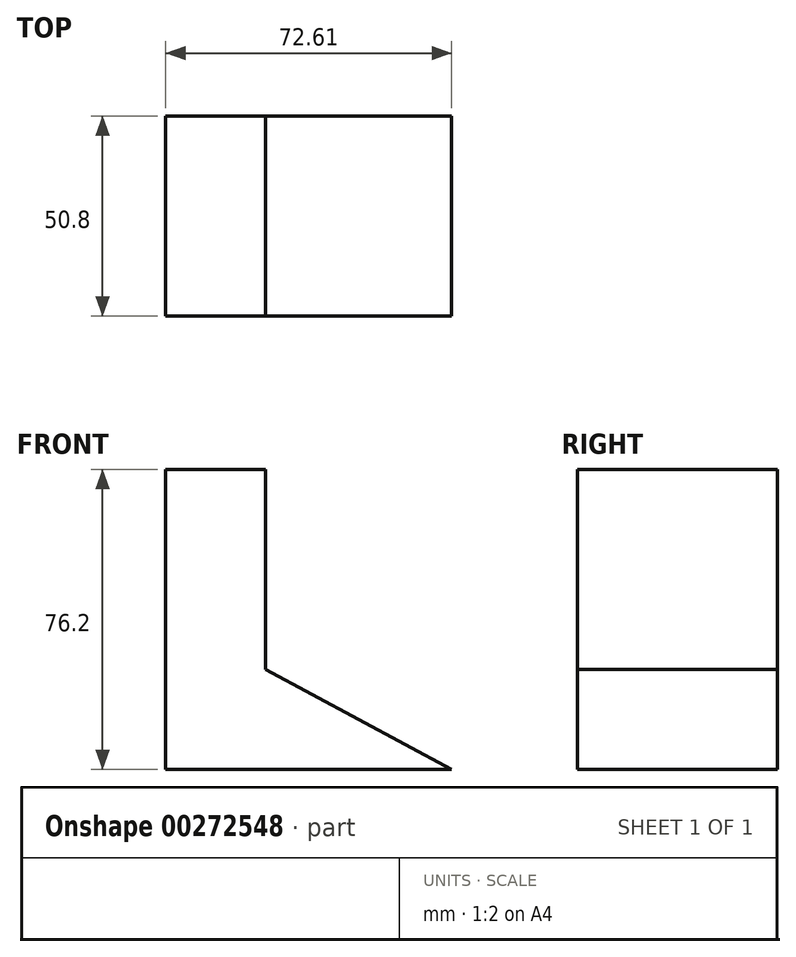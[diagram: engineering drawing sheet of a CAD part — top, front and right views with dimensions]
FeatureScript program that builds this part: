
annotation { "Feature Type Name" : "Feature", "Feature Type Description" : "" }
export const myFeature = defineFeature(function(context is Context, id is Id, definition is map)
    precondition{}
    {
        {
            var Q0;
            Q0=qCreatedBy(makeId("Front.planeOp"),FACE);
            var sketch = newSketch(context, id + "F0", { "sketchPlane" : qUnion([Q0])});
            skLineSegment(sketch, "E0", {"start": v(0, 0) * mm, "end": v(50.8, 0) * mm});
            skLineSegment(sketch, "E1", {"start": v(0, 0) * mm, "end": v(0, 76.2) * mm});
            skLineSegment(sketch, "E2", {"start": v(0, 76.2) * mm, "end": v(25.4, 76.2) * mm});
            skLineSegment(sketch, "E3", {"start": v(25.4, 76.2) * mm, "end": v(25.4, 25.4) * mm});
            skLineSegment(sketch, "E4", {"start": v(25.4, 25.4) * mm, "end": v(72.6, 0) * mm});
            skLineSegment(sketch, "E5", {"start": v(72.6, 0) * mm, "end": v(50.8, 0) * mm});
            skSolve(sketch);
        }
        {
            var Q0;
            Q0 = qSketchRegion(id + "F0", true);
            extrude(context, id + "F1", {"entities" : qUnion([Q0]), "depth" : 50.8 * mm});
        }
    });
